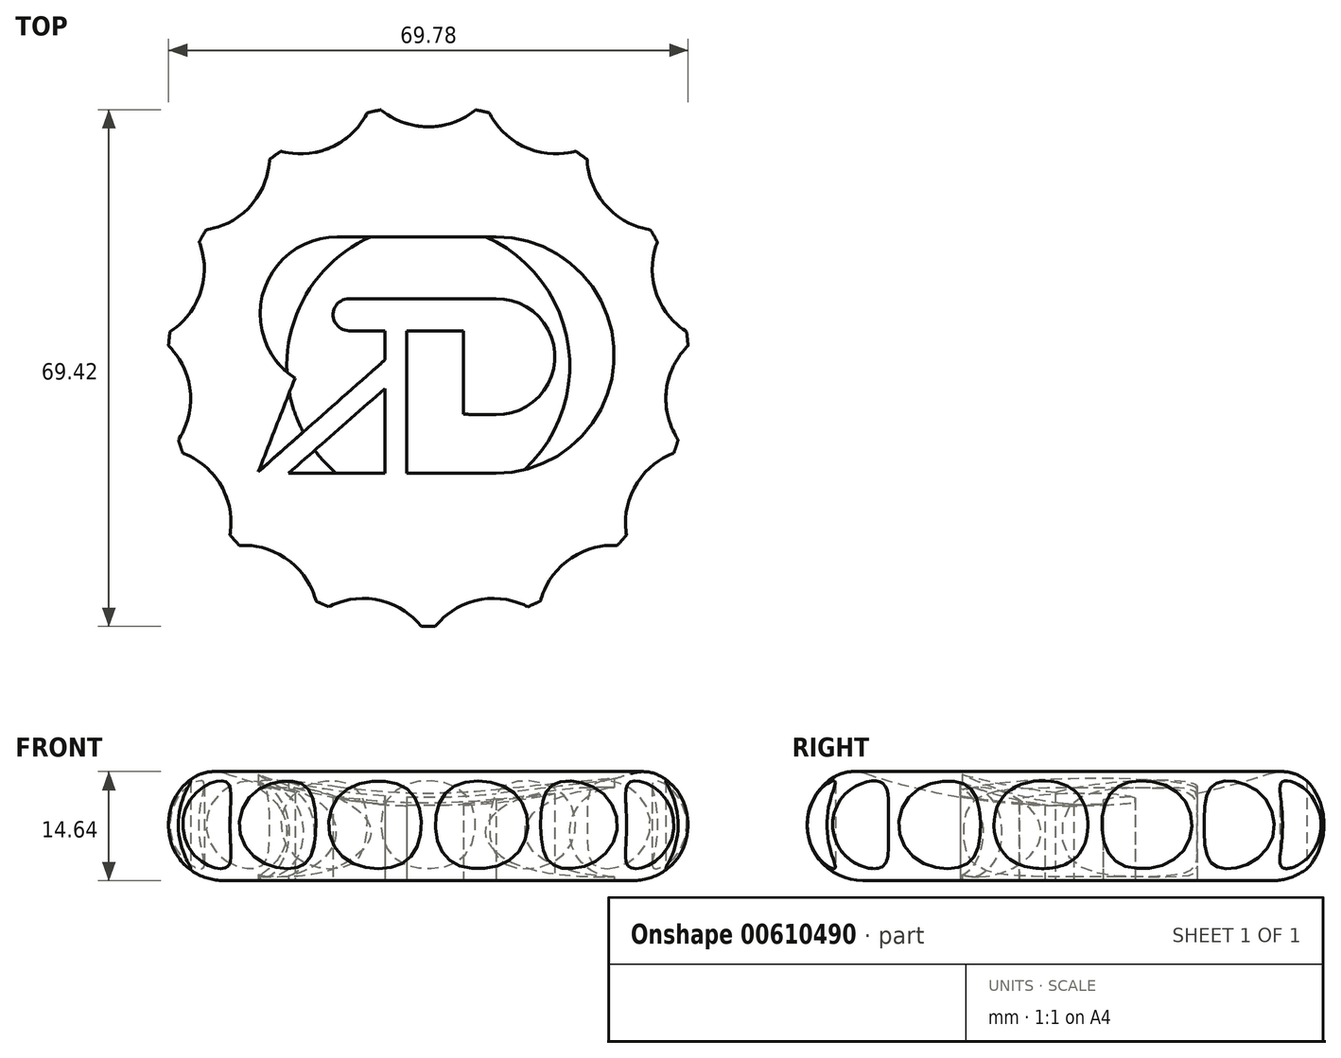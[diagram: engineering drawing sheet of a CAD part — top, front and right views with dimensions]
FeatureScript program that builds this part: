
annotation { "Feature Type Name" : "Feature", "Feature Type Description" : "" }
export const myFeature = defineFeature(function(context is Context, id is Id, definition is map)
    precondition{}
    {
        {
            var Q0;
            Q0=qCreatedBy(makeId("Top.planeOp"),FACE);
            var sketch = newSketch(context, id + "F0", { "sketchPlane" : qUnion([Q0])});
            skCircle(sketch, "E0", {"center": v(0, 0) * mm, "radius": 35 * mm});
            skSolve(sketch);
        }
        {
            var Q0;
            Q0=makeQuery(id+"F0.imprint","IMPRINT",FACE,{"disambiguationData":[TD([[makeQuery(id+"F0.imprint","IMPRINT",EDGE,{"derivedFrom":sQuery(id+"F0.wireOp",EDGE,"E0")}),1.0]])]});
            extrude(context, id + "F1", {"entities" : qUnion([Q0]), "depth" : 15 * mm, "offsetDistance" : 25 * mm});
        }
        {
            var Q0;
            Q0=makeQuery(id+"F1.opExtrude","CAP_FACE",FACE,{"disambiguationData":[OSD([sQuery(id+"F0.wireOp",EDGE,"E0")])],"isStart":false});
            var Q1;
            Q1=makeQuery(id+"F1.opExtrude","CAP_FACE",FACE,{"disambiguationData":[OSD([sQuery(id+"F0.wireOp",EDGE,"E0")])],"isStart":true});
            fillet(context, id + "F2", {"entities" : qUnion([Q0, Q1]), "radius" : 7.5 * mm, "tangentPropagation" : true, "allowEdgeOverflow" : false});
        }
        {
            var Q0;
            Q0=qCreatedBy(makeId("Front.planeOp"),FACE);
            var sketch = newSketch(context, id + "F3", { "sketchPlane" : qUnion([Q0])});
            skLineSegment(sketch, "E1", {"start": v(0, 0) * mm, "end": v(-30, 0) * mm});
            skLineSegment(sketch, "E2", {"start": v(-29, 15) * mm, "end": v(0, 15) * mm});
            skLineSegment(sketch, "E3", {"start": v(0, 15) * mm, "end": v(0, 10) * mm});
            skPoint(sketch, "E3.endSnap0", {"position": v(0, 15) * mm});
            skArc(sketch, "E4", {"start": v(-29, 15) * mm, "mid": v(-14.71, 11.26) * mm, "end": v(0, 10) * mm});
            skSolve(sketch);
        }
        {
            var Q0;
            Q0=qCreatedBy(makeId("Top.planeOp"),FACE);
            var sketch = newSketch(context, id + "F4", { "sketchPlane" : qUnion([Q0])});
            skLineSegment(sketch, "E5", {"start": v(-12.21, 17.37) * mm, "end": v(9.08, 17.37) * mm});
            skArc(sketch, "E6", {"start": v(9.08, -14.41) * mm, "mid": v(24.97, 1.48) * mm, "end": v(9.08, 17.37) * mm});
            skArc(sketch, "E7", {"start": v(9.08, -6.55) * mm, "mid": v(17, 1.25) * mm, "end": v(9.08, 9.05) * mm});
            skLineSegment(sketch, "E8", {"start": v(-17.9, -1.66) * mm, "end": v(-22.8, -14.19) * mm});
            skLineSegment(sketch, "E9", {"start": v(-22.8, -14.19) * mm, "end": v(-5.82, 0.82) * mm});
            skLineSegment(sketch, "E10", {"start": v(-5.82, 4.72) * mm, "end": v(-10.62, 4.72) * mm});
            skLineSegment(sketch, "E11", {"start": v(9.08, 9.05) * mm, "end": v(6.35, 9.05) * mm});
            skLineSegment(sketch, "E12", {"start": v(-10.62, 9.05) * mm, "end": v(6.35, 9.05) * mm});
            skLineSegment(sketch, "E13", {"start": v(9.08, -6.55) * mm, "end": v(4.75, -6.49) * mm});
            skLineSegment(sketch, "E14", {"start": v(4.75, -6.49) * mm, "end": v(4.75, 4.72) * mm});
            skLineSegment(sketch, "E15", {"start": v(4.75, 4.72) * mm, "end": v(-2.9, 4.72) * mm});
            skLineSegment(sketch, "E16", {"start": v(-2.9, -14.41) * mm, "end": v(9.08, -14.41) * mm});
            skLineSegment(sketch, "E17", {"start": v(-18.77, -14.41) * mm, "end": v(-5.82, -14.41) * mm});
            skLineSegment(sketch, "E18", {"start": v(-5.82, -14.41) * mm, "end": v(-5.82, -3.03) * mm});
            skArc(sketch, "E19", {"start": v(-10.62, 9.05) * mm, "mid": v(-12.78, 6.89) * mm, "end": v(-10.62, 4.72) * mm});
            skArc(sketch, "E20", {"start": v(-12.21, 17.37) * mm, "mid": v(-22.14, 9.97) * mm, "end": v(-17.9, -1.66) * mm});
            skPoint(sketch, "E21.start.orphan", {"position": v(-21.04, -14.41) * mm});
            skLineSegment(sketch, "E22", {"start": v(-5.82, 0.82) * mm, "end": v(-5.82, 4.72) * mm});
            skPoint(sketch, "E23.end.orphan", {"position": v(-5.27, 4.72) * mm});
            skLineSegment(sketch, "E24.0", {"start": v(-2.9, 4.72) * mm, "end": v(-2.9, -14.41) * mm});
            skPoint(sketch, "E25.orphan", {"position": v(-3.9, -14.41) * mm});
            skLineSegment(sketch, "E26.0", {"start": v(-5.82, -3.03) * mm, "end": v(-18.77, -14.41) * mm});
            skSolve(sketch);
        }
        {
            var Q0;
            Q0=qSketchRegion(id+"F4",true);
            var Q1;
            Q1=qConstructionFilter(qBodyType(qCreatedBy(id+"F4",EDGE),BodyType.WIRE),ConstructionObject.NO);
            extrude(context, id + "F5", {"entities" : qUnion([Q0]), "operationType" : NewBodyOperationType.REMOVE, "surfaceEntities" : qUnion([Q1]), "depth" : 25 * mm, "offsetDistance" : 25 * mm});
        }
        {
            var Q0;
            Q0=qSketchRegion(id+"F3",true);
            var Q1;
            {var subQ0=sQuery(id+"F0.wireOp",EDGE,"E0");Q1=makeQuery(id+"F2.opFillet","BLEND_FACE",FACE,{"disambiguationData":[OSD([subQ0]),TDD([makeQuery(id+"F1.opExtrude","CAP_EDGE",EDGE,{"disambiguationData":[OSD([subQ0])],"isStart":true})])]});}
            revolve(context, id + "F6", {"operationType" : NewBodyOperationType.REMOVE, "entities" : qUnion([Q0]), "axis" : qUnion([Q1]), "revolveType" : RevolveType.FULL, "oppositeDirection" : true});
        }
        {
            var Q0;
            Q0=makeQuery(id+"F6.boolean.opBoolean","INTERSECT",EDGE,{"derivedFrom":[makeQuery(id+"F2.opFillet","BLEND_FACE",FACE,{"disambiguationData":[OSD([sQuery(id+"F0.wireOp",EDGE,"E0")])]}),makeQuery(id+"F6.opRevolve","SWEPT_FACE",FACE,{"disambiguationData":[OSD([sQuery(id+"F3.wireOp",EDGE,"E4")])]})]});
            fillet(context, id + "F7", {"entities" : qUnion([Q0]), "radius" : 5 * mm, "tangentPropagation" : true, "allowEdgeOverflow" : false});
        }
        {
            var Q0;
            Q0=qCreatedBy(makeId("Top.planeOp"),FACE);
            var sketch = newSketch(context, id + "F8", { "sketchPlane" : qUnion([Q0])});
            skCircle(sketch, "E27", {"center": v(0, 0) * mm, "radius": 35 * mm, "construction": true});
            skLineSegment(sketch, "E28", {"start": v(0, 35) * mm, "end": v(-7, 35) * mm});
            skLineSegment(sketch, "E29", {"start": v(0, 35) * mm, "end": v(7, 35) * mm});
            skArc(sketch, "E30", {"start": v(-7, 35) * mm, "mid": v(0, 32.14) * mm, "end": v(7, 35) * mm});
            skLineSegment(sketch, "E31.1.0", {"start": v(-14.24, 31.97) * mm, "end": v(-20.63, 29.13) * mm});
            skLineSegment(sketch, "E31.1.1", {"start": v(-14.24, 31.97) * mm, "end": v(-7.84, 34.82) * mm});
            skArc(sketch, "E31.1.2", {"start": v(-20.63, 29.13) * mm, "mid": v(-13.07, 29.36) * mm, "end": v(-7.84, 34.82) * mm});
            skLineSegment(sketch, "E31.2.0", {"start": v(-26.01, 23.42) * mm, "end": v(-30.7, 18.22) * mm});
            skLineSegment(sketch, "E31.2.1", {"start": v(-26.01, 23.42) * mm, "end": v(-21.33, 28.62) * mm});
            skArc(sketch, "E31.2.2", {"start": v(-30.7, 18.22) * mm, "mid": v(-23.89, 21.5) * mm, "end": v(-21.33, 28.62) * mm});
            skLineSegment(sketch, "E31.3.0", {"start": v(-33.29, 10.82) * mm, "end": v(-35.45, 4.16) * mm});
            skLineSegment(sketch, "E31.3.1", {"start": v(-33.29, 10.82) * mm, "end": v(-31.12, 17.47) * mm});
            skArc(sketch, "E31.3.2", {"start": v(-35.45, 4.16) * mm, "mid": v(-30.57, 9.93) * mm, "end": v(-31.12, 17.47) * mm});
            skLineSegment(sketch, "E31.4.0", {"start": v(-34.8, -3.66) * mm, "end": v(-34.08, -10.62) * mm});
            skLineSegment(sketch, "E31.4.1", {"start": v(-34.8, -3.66) * mm, "end": v(-35.54, 3.3) * mm});
            skArc(sketch, "E31.4.2", {"start": v(-34.08, -10.62) * mm, "mid": v(-31.97, -3.36) * mm, "end": v(-35.54, 3.3) * mm});
            skLineSegment(sketch, "E31.5.0", {"start": v(-30.31, -17.5) * mm, "end": v(-26.81, -23.56) * mm});
            skLineSegment(sketch, "E31.5.1", {"start": v(-30.31, -17.5) * mm, "end": v(-33.81, -11.44) * mm});
            skArc(sketch, "E31.5.2", {"start": v(-26.81, -23.56) * mm, "mid": v(-27.84, -16.07) * mm, "end": v(-33.81, -11.44) * mm});
            skLineSegment(sketch, "E31.6.0", {"start": v(-20.57, -28.32) * mm, "end": v(-14.9, -32.43) * mm});
            skLineSegment(sketch, "E31.6.1", {"start": v(-20.57, -28.32) * mm, "end": v(-26.24, -24.2) * mm});
            skArc(sketch, "E31.6.2", {"start": v(-14.9, -32.43) * mm, "mid": v(-18.9, -26) * mm, "end": v(-26.24, -24.2) * mm});
            skLineSegment(sketch, "E31.7.0", {"start": v(-7.28, -34.24) * mm, "end": v(-0.43, -35.7) * mm});
            skLineSegment(sketch, "E31.7.1", {"start": v(-7.28, -34.24) * mm, "end": v(-14.12, -32.78) * mm});
            skArc(sketch, "E31.7.2", {"start": v(-0.43, -35.7) * mm, "mid": v(-6.68, -31.44) * mm, "end": v(-14.12, -32.78) * mm});
            skLineSegment(sketch, "E31.8.0", {"start": v(7.28, -34.24) * mm, "end": v(14.12, -32.78) * mm});
            skLineSegment(sketch, "E31.8.1", {"start": v(7.28, -34.24) * mm, "end": v(0.43, -35.7) * mm});
            skArc(sketch, "E31.8.2", {"start": v(14.12, -32.78) * mm, "mid": v(6.68, -31.44) * mm, "end": v(0.43, -35.7) * mm});
            skLineSegment(sketch, "E31.9.0", {"start": v(20.57, -28.32) * mm, "end": v(26.24, -24.2) * mm});
            skLineSegment(sketch, "E31.9.1", {"start": v(20.57, -28.32) * mm, "end": v(14.9, -32.43) * mm});
            skArc(sketch, "E31.9.2", {"start": v(26.24, -24.2) * mm, "mid": v(18.9, -26) * mm, "end": v(14.9, -32.43) * mm});
            skLineSegment(sketch, "E31.10.0", {"start": v(30.31, -17.5) * mm, "end": v(33.81, -11.44) * mm});
            skLineSegment(sketch, "E31.10.1", {"start": v(30.31, -17.5) * mm, "end": v(26.81, -23.56) * mm});
            skArc(sketch, "E31.10.2", {"start": v(33.81, -11.44) * mm, "mid": v(27.84, -16.07) * mm, "end": v(26.81, -23.56) * mm});
            skLineSegment(sketch, "E31.11.0", {"start": v(34.8, -3.66) * mm, "end": v(35.54, 3.3) * mm});
            skLineSegment(sketch, "E31.11.1", {"start": v(34.8, -3.66) * mm, "end": v(34.08, -10.62) * mm});
            skArc(sketch, "E31.11.2", {"start": v(35.54, 3.3) * mm, "mid": v(31.97, -3.36) * mm, "end": v(34.08, -10.62) * mm});
            skLineSegment(sketch, "E31.12.0", {"start": v(33.29, 10.82) * mm, "end": v(31.12, 17.47) * mm});
            skLineSegment(sketch, "E31.12.1", {"start": v(33.29, 10.82) * mm, "end": v(35.45, 4.16) * mm});
            skArc(sketch, "E31.12.2", {"start": v(31.12, 17.47) * mm, "mid": v(30.57, 9.93) * mm, "end": v(35.45, 4.16) * mm});
            skLineSegment(sketch, "E31.13.0", {"start": v(26.01, 23.42) * mm, "end": v(21.33, 28.62) * mm});
            skLineSegment(sketch, "E31.13.1", {"start": v(26.01, 23.42) * mm, "end": v(30.7, 18.22) * mm});
            skArc(sketch, "E31.13.2", {"start": v(21.33, 28.62) * mm, "mid": v(23.89, 21.5) * mm, "end": v(30.7, 18.22) * mm});
            skLineSegment(sketch, "E31.14.0", {"start": v(14.24, 31.97) * mm, "end": v(7.84, 34.82) * mm});
            skLineSegment(sketch, "E31.14.1", {"start": v(14.24, 31.97) * mm, "end": v(20.63, 29.13) * mm});
            skArc(sketch, "E31.14.2", {"start": v(7.84, 34.82) * mm, "mid": v(13.07, 29.36) * mm, "end": v(20.63, 29.13) * mm});
            skSolve(sketch);
        }
        {
            var Q0;
            Q0=qSketchRegion(id+"F8",true);
            extrude(context, id + "F9", {"entities" : qUnion([Q0]), "operationType" : NewBodyOperationType.REMOVE, "depth" : 25 * mm, "offsetDistance" : 25 * mm});
        }
        {
            var Q0;
            Q0=qCreatedBy(makeId("Front.planeOp"),FACE);
            var sketch = newSketch(context, id + "F10", { "sketchPlane" : qUnion([Q0])});
            skCircle(sketch, "E32", {"center": v(-25, 6.5) * mm, "radius": 6 * mm});
            skSolve(sketch);
        }
        {
            var Q0;
            Q0=qSketchRegion(id+"F10",true);
            var Q1;
            {var subQ0=makeQuery(id+"F2.opFillet","BLEND_FACE",FACE,{"disambiguationData":[OSD([sQuery(id+"F0.wireOp",EDGE,"E0")])]});Q1=makeQuery(id+"F7.opFillet","BLEND_EDGE",EDGE,{"blendedFrom":[makeQuery(id+"F6.boolean.opBoolean","INTERSECT",EDGE,{"derivedFrom":[subQ0,makeQuery(id+"F6.opRevolve","SWEPT_FACE",FACE,{"disambiguationData":[OSD([sQuery(id+"F3.wireOp",EDGE,"E4")])]})]}),subQ0],"blendedInto":[subQ0]});}
            revolve(context, id + "F11", {"operationType" : NewBodyOperationType.ADD, "entities" : qUnion([Q0]), "axis" : qUnion([Q1]), "revolveType" : RevolveType.FULL});
        }
    });
